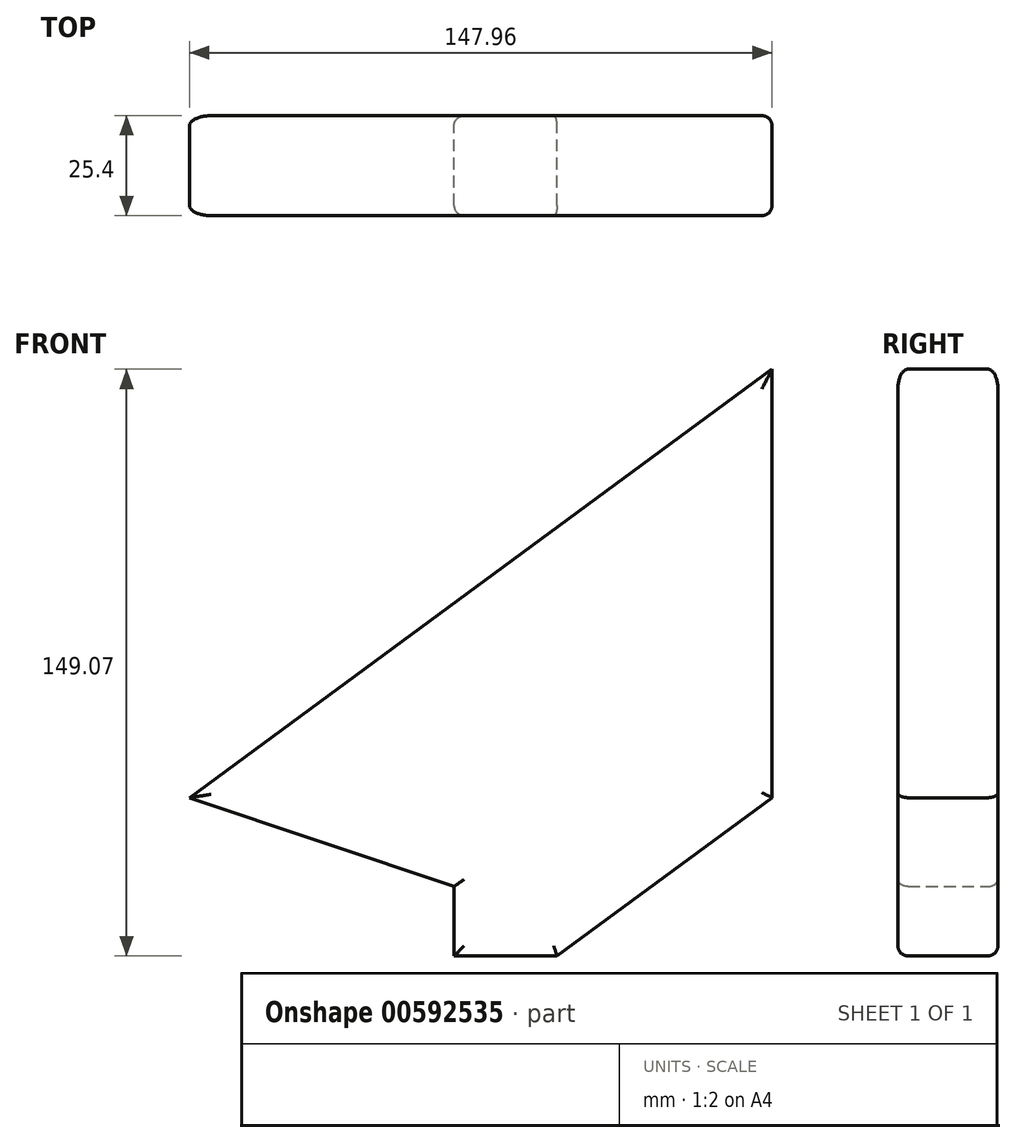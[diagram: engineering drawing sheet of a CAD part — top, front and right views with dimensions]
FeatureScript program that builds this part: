
annotation { "Feature Type Name" : "Feature", "Feature Type Description" : "" }
export const myFeature = defineFeature(function(context is Context, id is Id, definition is map)
    precondition{}
    {
        {
            var Q0;
            Q0=qCreatedBy(makeId("Front.planeOp"),FACE);
            var sketch = newSketch(context, id + "F0", { "sketchPlane" : qUnion([Q0])});
            skLineSegment(sketch, "E0", {"start": v(0, 0) * mm, "end": v(147.96, 108.9) * mm});
            skLineSegment(sketch, "E1", {"start": v(147.96, 108.9) * mm, "end": v(147.96, 0) * mm});
            skLineSegment(sketch, "E2", {"start": v(147.96, 0) * mm, "end": v(93.36, -40.18) * mm});
            skLineSegment(sketch, "E3", {"start": v(93.36, -40.18) * mm, "end": v(67.2, -40.18) * mm});
            skLineSegment(sketch, "E4", {"start": v(67.2, -40.18) * mm, "end": v(67.2, -22.55) * mm});
            skLineSegment(sketch, "E5", {"start": v(67.2, -22.55) * mm, "end": v(0, 0) * mm});
            skSolve(sketch);
        }
        {
            var Q0;
            Q0=makeQuery(id+"F0.imprint","IMPRINT",FACE,{"disambiguationData":[TD([[makeQuery(id+"F0.imprint","IMPRINT",EDGE,{"derivedFrom":sQuery(id+"F0.wireOp",EDGE,"E0")}),-1.0]])]});
            extrude(context, id + "F1", {"entities" : qUnion([Q0]), "depth" : 25.4 * mm, "offsetDistance" : 25.4 * mm});
        }
        {
            var Q0;
            Q0=makeQuery(id+"F1.opExtrude","CAP_FACE",FACE,{"disambiguationData":[OSD([sQuery(id+"F0.wireOp",EDGE,"E0"),sQuery(id+"F0.wireOp",EDGE,"E1"),sQuery(id+"F0.wireOp",EDGE,"E2"),sQuery(id+"F0.wireOp",EDGE,"E3"),sQuery(id+"F0.wireOp",EDGE,"E4"),sQuery(id+"F0.wireOp",EDGE,"E5")])],"isStart":false});
            var Q1;
            Q1=makeQuery(id+"F1.opExtrude","CAP_FACE",FACE,{"disambiguationData":[OSD([sQuery(id+"F0.wireOp",EDGE,"E0"),sQuery(id+"F0.wireOp",EDGE,"E1"),sQuery(id+"F0.wireOp",EDGE,"E2"),sQuery(id+"F0.wireOp",EDGE,"E3"),sQuery(id+"F0.wireOp",EDGE,"E4"),sQuery(id+"F0.wireOp",EDGE,"E5")])],"isStart":true});
            fillet(context, id + "F2", {"entities" : qUnion([Q0, Q1]), "radius" : 2.54 * mm, "tangentPropagation" : true, "allowEdgeOverflow" : false});
        }
    });
